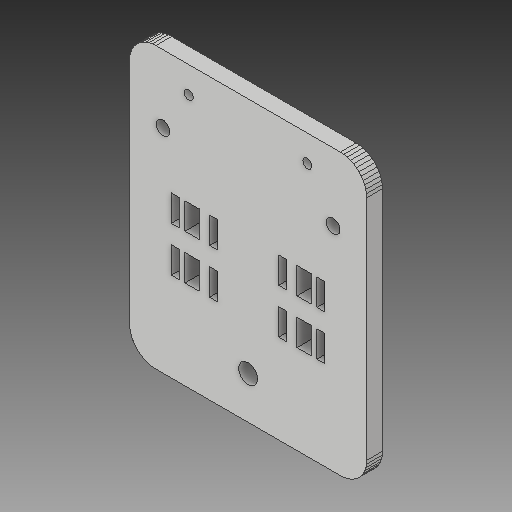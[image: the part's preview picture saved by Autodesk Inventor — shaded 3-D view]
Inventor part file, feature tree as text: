
AUTODESK INVENTOR PART (.ipt)
format: ipt  version: 2018 (Build 220112000, 112)  size: 312,320 bytes
history: native  units: mm
features: sketch x4, other x3
ambient origin geometry x8: Origin, YZ Plane, XZ Plane, XY Plane, X Axis, Y Axis, Z Axis, Center Point
bodies: Solid1 (feature_tree)
feature tree (7):
  other  "X-Axis-End-Plate_MIR.ipt"
  other  "Solid1::X-Axis-End-Plate_MIR.ipt"
  other  "TaggingFeature1"
  sketch  "Sketch1"  dims[d0=10.0mm]
  sketch  "Sketch2"
  sketch  "Sketch3"
  sketch  "Sketch4"
